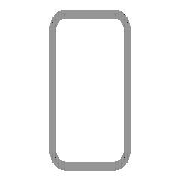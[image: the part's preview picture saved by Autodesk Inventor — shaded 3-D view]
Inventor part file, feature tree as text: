
AUTODESK INVENTOR PART (.ipt)
format: ipt  version: 2025.3 (Build 293356000, 356)  size: 136,704 bytes
history: native  units: mm (DEFAULTED — no unit token found)
features: other x4, sketch x1, plane x1
ambient origin geometry x8: Origin, YZ Plane, XZ Plane, XY Plane, X Axis, Y Axis, Z Axis, Center Point
bodies: Solid1 (feature_tree), Body (feature_tree)
feature tree (6):
  parser-record x1  (decoder bookkeeping rows leaked as tree rows — omitted from the tree; the rows remain in map.json)
  other  "Driven Length"
  other  "Start Plane"
  other  "End Plane"
  sketch  "Sketch3"  dims[d3=2040.0mm d4=0.0mm d7=6.0mm d9=40.0mm d11=80.0mm d12=3.0mm d13=80.0mm d14=2120.0mm d15=20.0mm d16=40.0mm d17=90.0deg d18=2040.0mm]
  plane  "Work Plane3"
